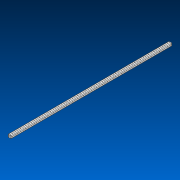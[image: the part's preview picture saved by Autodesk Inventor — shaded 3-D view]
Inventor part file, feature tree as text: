
AUTODESK INVENTOR PART (.ipt)
format: ipt  version: 2022.2 (Build 262287000, 287)  size: 1,043,968 bytes
history: native  units: in
note: dims shown in document units (in); Inventor stores cm internally (conversion verified against a paired STEP export)
features: other x118, pattern_linear x2, extrude x1, sketch x1
ambient origin geometry x8: Origin, YZ Plane, XZ Plane, XY Plane, X Axis, Y Axis, Z Axis, Center Point
bodies: Solid1 (feature_tree)
feature tree (122):
  extrude  "Extrusion1"  TaperAngle=0.0deg  [1 undecoded]
  other  "Work Axis1"
  other  "Work Axis2"
  pattern_linear  "Rectangular Pattern1"  Count1=59  [1 undecoded]
  pattern_linear  "Rectangular Pattern2"  Spacing1=1.0in  [1 undecoded]
  sketch  "Sketch1"  dims[d0=0.0in d1=0.0in d2=23.2283in d4=1.0in d5=22.8346in d7=1.0in]
  other  "Work Axis3"
  other  "Work Axis4"
  other  "Work Axis5"
  other  "Work Axis6"
  other  "Work Axis7"
  other  "Work Axis8"
  other  "Work Axis9"
  other  "Work Axis10"
  other  "Work Axis11"
  other  "Work Axis12"
  other  "Work Axis13"
  other  "Work Axis14"
  other  "Work Axis15"
  other  "Work Axis16"
  other  "Work Axis17"
  other  "Work Axis18"
  other  "Work Axis19"
  other  "Work Axis20"
  other  "Work Axis21"
  other  "Work Axis22"
  other  "Work Axis23"
  other  "Work Axis24"
  other  "Work Axis25"
  other  "Work Axis26"
  other  "Work Axis27"
  other  "Work Axis28"
  other  "Work Axis29"
  other  "Work Axis30"
  other  "Work Axis31"
  other  "Work Axis32"
  other  "Work Axis33"
  other  "Work Axis34"
  other  "Work Axis35"
  other  "Work Axis36"
  other  "Work Axis37"
  other  "Work Axis38"
  other  "Work Axis39"
  other  "Work Axis40"
  other  "Work Axis41"
  other  "Work Axis42"
  other  "Work Axis43"
  other  "Work Axis44"
  other  "Work Axis45"
  other  "Work Axis46"
  other  "Work Axis47"
  other  "Work Axis48"
  other  "Work Axis49"
  other  "Work Axis50"
  other  "Work Axis51"
  other  "Work Axis52"
  other  "Work Axis53"
  other  "Work Axis54"
  other  "Work Axis55"
  other  "Work Axis56"
  other  "Work Axis57"
  other  "Work Axis58"
  other  "Work Axis59"
  other  "Work Axis60"
  other  "Work Axis61"
  other  "Work Axis62"
  other  "Work Axis63"
  other  "Work Axis64"
  other  "Work Axis65"
  other  "Work Axis66"
  other  "Work Axis67"
  other  "Work Axis68"
  other  "Work Axis69"
  other  "Work Axis70"
  other  "Work Axis71"
  other  "Work Axis72"
  other  "Work Axis73"
  other  "Work Axis74"
  other  "Work Axis75"
  other  "Work Axis76"
  other  "Work Axis77"
  other  "Work Axis78"
  other  "Work Axis79"
  other  "Work Axis80"
  other  "Work Axis81"
  other  "Work Axis82"
  other  "Work Axis83"
  other  "Work Axis84"
  other  "Work Axis85"
  other  "Work Axis86"
  other  "Work Axis87"
  other  "Work Axis88"
  other  "Work Axis89"
  other  "Work Axis90"
  other  "Work Axis91"
  other  "Work Axis92"
  other  "Work Axis93"
  other  "Work Axis94"
  other  "Work Axis95"
  other  "Work Axis96"
  other  "Work Axis97"
  other  "Work Axis98"
  other  "Work Axis99"
  other  "Work Axis100"
  other  "Work Axis101"
  other  "Work Axis102"
  other  "Work Axis103"
  other  "Work Axis104"
  other  "Work Axis105"
  other  "Work Axis106"
  other  "Work Axis107"
  other  "Work Axis108"
  other  "Work Axis109"
  other  "Work Axis110"
  other  "Work Axis111"
  other  "Work Axis112"
  other  "Work Axis113"
  other  "Work Axis114"
  other  "Work Axis115"
  other  "Work Axis116"
  other  "Work Axis117"
  other  "LPattern2"
note: 3 required parameter values undecoded (feature->parameter linkage not recoverable at this tier; creation-order binding heuristic only, values carry confidence <= 0.55)
